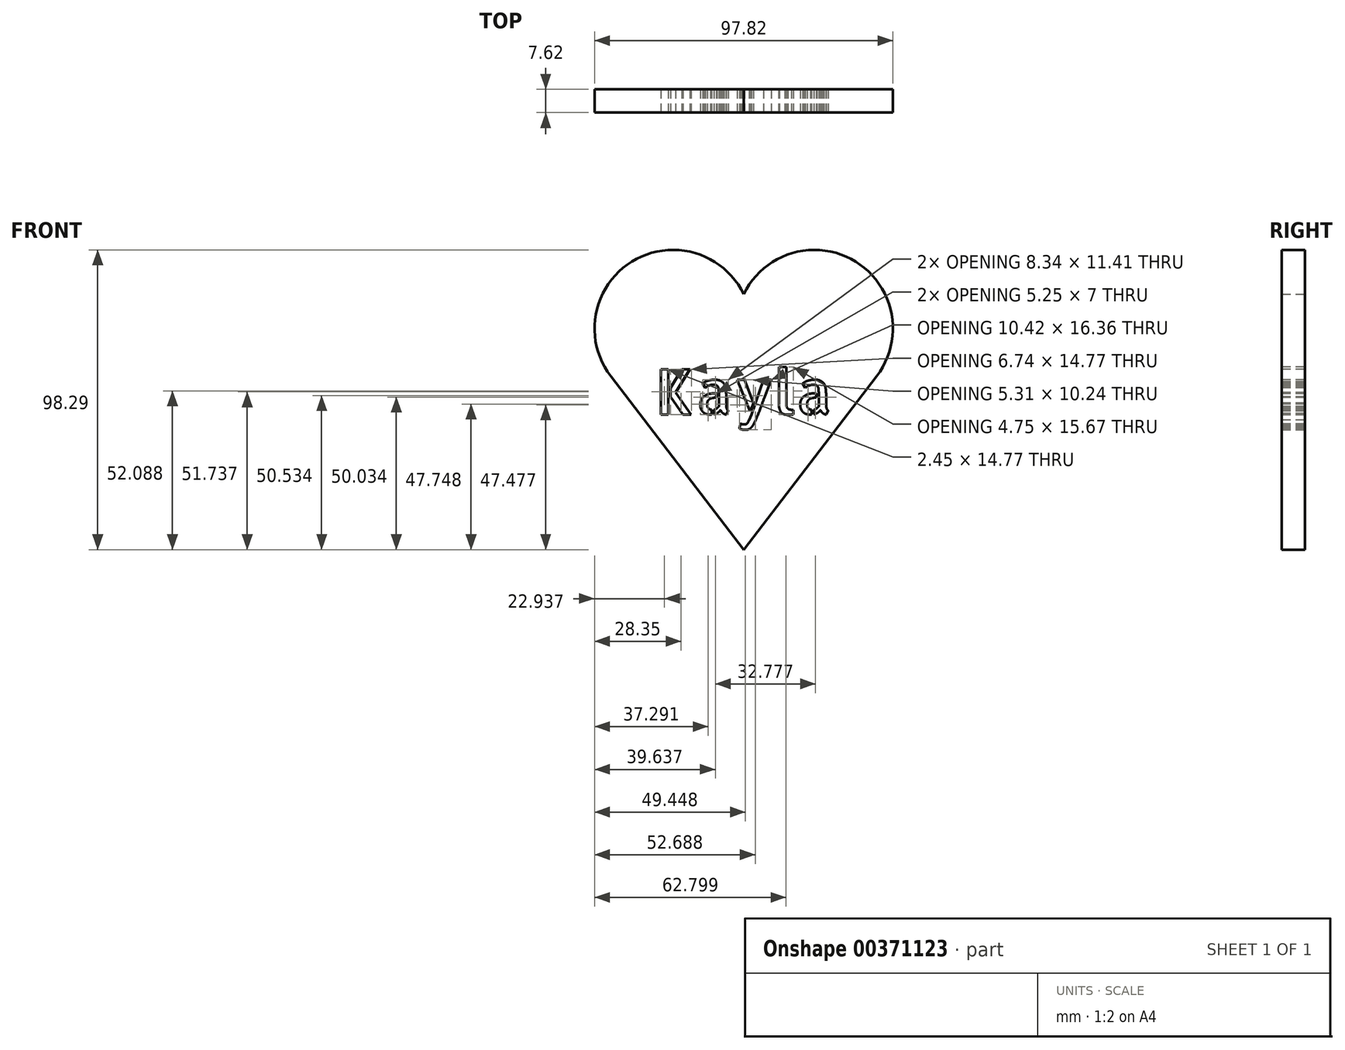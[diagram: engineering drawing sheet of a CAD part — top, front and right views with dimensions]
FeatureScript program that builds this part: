
annotation { "Feature Type Name" : "Feature", "Feature Type Description" : "" }
export const myFeature = defineFeature(function(context is Context, id is Id, definition is map)
    precondition{}
    {
        {
            var Q0;
            Q0=qCreatedBy(makeId("Front.planeOp"),FACE);
            var sketch = newSketch(context, id + "F0", { "sketchPlane" : qUnion([Q0])});
            skArc(sketch, "E0", {"start": v(43.6, 12.53) * mm, "mid": v(36.69, 50.1) * mm, "end": v(0, 39.44) * mm});
            skLineSegment(sketch, "E1", {"start": v(0, -44.35) * mm, "end": v(43.6, 12.53) * mm});
            skArc(sketch, "E2.MirrorCS", {"start": v(-43.6, 12.53) * mm, "mid": v(-36.69, 50.1) * mm, "end": v(0, 39.44) * mm});
            skLineSegment(sketch, "E3.MirrorCS", {"start": v(0, -44.35) * mm, "end": v(-43.6, 12.53) * mm});
            skSolve(sketch);
        }
        {
            var Q0;
            Q0 = qSketchRegion(id + "F0", true);
            extrude(context, id + "F1", {"entities" : qUnion([Q0]), "depth" : 7.62 * mm});
        }
        {
            var Q0;
            Q0=makeQuery(id+"F1.opExtrude","CAP_FACE",FACE,{"disambiguationData":[OSD([sQuery(id+"F0.wireOp",EDGE,"E0"),sQuery(id+"F0.wireOp",EDGE,"E1"),sQuery(id+"F0.wireOp",EDGE,"E2.MirrorCS"),sQuery(id+"F0.wireOp",EDGE,"E3.MirrorCS")])],"isStart":false});
            var sketch = newSketch(context, id + "F2", { "sketchPlane" : qUnion([Q0])});
            skText(sketch, "E4", { "text": "Kayla", "fontName": "AllertaStencil-Regular.ttf"});
            const initialGuessF2  = {"E4": [-0.02906, 0, 1, 0, 0.01478]};
            skSetInitialGuess(sketch, initialGuessF2);
            skSolve(sketch);
        }
        {
            var Q0;
            Q0 = qSketchRegion(id + "F2", true);
            extrude(context, id + "F3", {"entities" : qUnion([Q0]), "operationType" : NewBodyOperationType.REMOVE, "oppositeDirection" : true, "depth" : 7.62 * mm});
        }
    });
